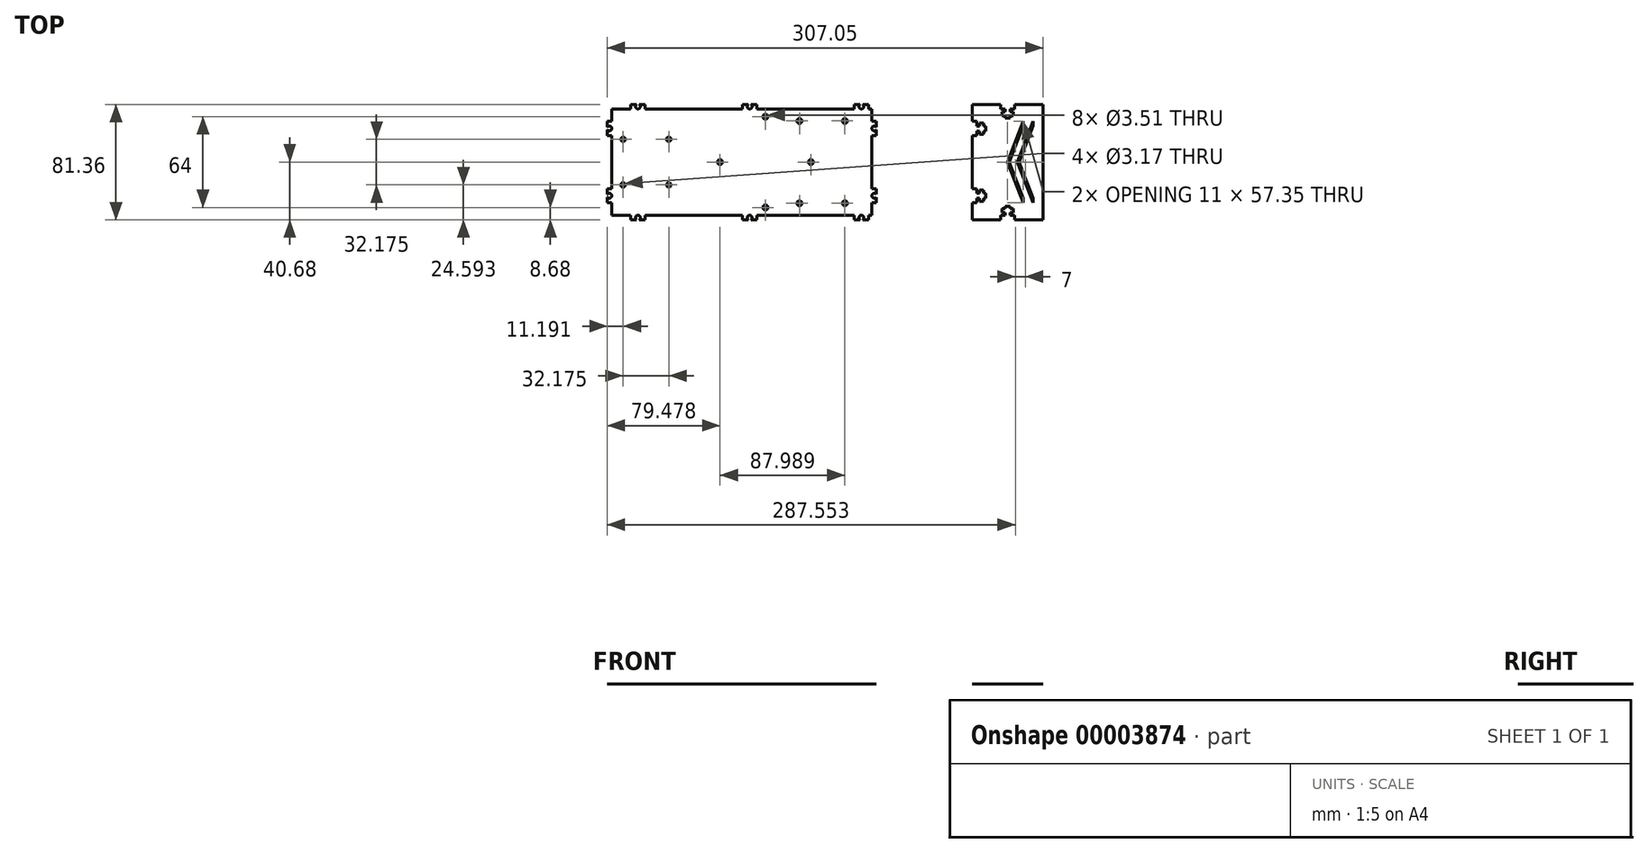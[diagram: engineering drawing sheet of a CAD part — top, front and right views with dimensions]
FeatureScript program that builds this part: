
annotation { "Feature Type Name" : "Feature", "Feature Type Description" : "" }
export const myFeature = defineFeature(function(context is Context, id is Id, definition is map)
    precondition{}
    {
        {
            var Q0;
            Q0=qCreatedBy(makeId("Top.planeOp"),FACE);
            var sketch = newSketch(context, id + "F0", { "sketchPlane" : qUnion([Q0])});
            skLineSegment(sketch, "E0", {"start": v(-129.35, 56.25) * mm, "end": v(-115.88, 56.25) * mm});
            skLineSegment(sketch, "E1", {"start": v(53.99, 56.25) * mm, "end": v(53.99, 47.48) * mm});
            skLineSegment(sketch, "E2", {"start": v(-129.35, 56.25) * mm, "end": v(-129.35, 47.48) * mm});
            skLineSegment(sketch, "E3", {"start": v(-129.35, -18.75) * mm, "end": v(-115.88, -18.75) * mm});
            skPoint(sketch, "E4", {"position": v(-129.35, 18.75) * mm});
            skLineSegment(sketch, "E5", {"start": v(-129.35, 18.75) * mm, "end": v(53.99, 18.75) * mm, "construction": true});
            skPoint(sketch, "E6", {"position": v(-129.35, 37.5) * mm});
            skPoint(sketch, "E7", {"position": v(-129.35, 0) * mm});
            skPoint(sketch, "E8", {"position": v(-129.35, 33.46) * mm});
            skPoint(sketch, "E9", {"position": v(-129.35, 1.3) * mm});
            skPoint(sketch, "E10", {"position": v(-129.35, 56.25) * mm});
            skPoint(sketch, "E11", {"position": v(-129.35, 59.42) * mm});
            skPoint(sketch, "E12", {"position": v(-129.35, -18.75) * mm});
            skPoint(sketch, "E13", {"position": v(-129.35, -21.93) * mm});
            skLineSegment(sketch, "E14", {"start": v(-129.35, 59.42) * mm, "end": v(66.84, 59.42) * mm, "construction": true});
            skPoint(sketch, "E15", {"position": v(-115.88, 56.25) * mm});
            skPoint(sketch, "E16", {"position": v(-105.88, 56.25) * mm});
            skPoint(sketch, "E17", {"position": v(-110.88, 56.25) * mm});
            skArc(sketch, "E18", {"start": v(-111.9, 59.42) * mm, "mid": v(-110.88, 56.25) * mm, "end": v(-109.85, 59.42) * mm});
            skLineSegment(sketch, "E19", {"start": v(-110.88, 58) * mm, "end": v(-110.88, 56.25) * mm});
            skLineSegment(sketch, "E20", {"start": v(-115.88, 56.25) * mm, "end": v(-115.88, 59.42) * mm});
            skLineSegment(sketch, "E21", {"start": v(-115.88, 59.42) * mm, "end": v(-111.9, 59.42) * mm});
            skLineSegment(sketch, "E22", {"start": v(-105.88, 56.25) * mm, "end": v(-105.88, 59.42) * mm});
            skLineSegment(sketch, "E23.trimOffspring", {"start": v(-109.85, 59.42) * mm, "end": v(-105.88, 59.42) * mm});
            skLineSegment(sketch, "E24.0.MirrorCS", {"start": v(-115.88, -18.75) * mm, "end": v(-115.88, -21.93) * mm});
            skLineSegment(sketch, "E25.0.MirrorCS", {"start": v(-115.88, -21.92) * mm, "end": v(-111.9, -21.92) * mm});
            skArc(sketch, "E26.0.MirrorCS", {"start": v(-111.9, -21.93) * mm, "mid": v(-110.88, -18.75) * mm, "end": v(-109.85, -21.93) * mm});
            skLineSegment(sketch, "E27.0.MirrorCS", {"start": v(-109.85, -21.92) * mm, "end": v(-105.88, -21.92) * mm});
            skLineSegment(sketch, "E28.0.MirrorCS", {"start": v(-105.88, -18.75) * mm, "end": v(-105.88, -21.93) * mm});
            skLineSegment(sketch, "E29.trimOffspring", {"start": v(-105.88, 56.25) * mm, "end": v(-37.16, 56.25) * mm});
            skLineSegment(sketch, "E30.trimOffspring", {"start": v(-105.88, -18.75) * mm, "end": v(-37.16, -18.75) * mm});
            skLineSegment(sketch, "E31.1.0.0", {"start": v(-37.16, 56.25) * mm, "end": v(-37.16, 59.42) * mm});
            skLineSegment(sketch, "E31.1.0.1", {"start": v(-37.16, 59.42) * mm, "end": v(-33.18, 59.42) * mm});
            skArc(sketch, "E31.1.0.2", {"start": v(-33.18, 59.42) * mm, "mid": v(-32.16, 56.25) * mm, "end": v(-31.14, 59.42) * mm});
            skLineSegment(sketch, "E31.1.0.3", {"start": v(-31.14, 59.42) * mm, "end": v(-27.16, 59.42) * mm});
            skLineSegment(sketch, "E31.1.0.4", {"start": v(-27.16, 56.25) * mm, "end": v(-27.16, 59.42) * mm});
            skLineSegment(sketch, "E31.2.0.0", {"start": v(41.56, 56.25) * mm, "end": v(41.56, 59.42) * mm});
            skLineSegment(sketch, "E31.2.0.1", {"start": v(41.56, 59.42) * mm, "end": v(45.53, 59.42) * mm});
            skArc(sketch, "E31.2.0.2", {"start": v(45.53, 59.42) * mm, "mid": v(46.56, 56.25) * mm, "end": v(47.58, 59.42) * mm});
            skLineSegment(sketch, "E31.2.0.3", {"start": v(47.58, 59.42) * mm, "end": v(51.56, 59.42) * mm});
            skLineSegment(sketch, "E31.2.0.4", {"start": v(51.56, 56.25) * mm, "end": v(51.56, 59.42) * mm});
            skLineSegment(sketch, "E31.direction1", {"start": v(-115.88, 56.25) * mm, "end": v(-37.16, 56.25) * mm, "construction": true});
            skLineSegment(sketch, "E32.trimOffspring", {"start": v(-27.16, 56.25) * mm, "end": v(41.56, 56.25) * mm});
            skLineSegment(sketch, "E33.trimOffspring", {"start": v(51.56, 56.25) * mm, "end": v(53.99, 56.25) * mm});
            skLineSegment(sketch, "E34.0.MirrorCS", {"start": v(-37.16, -18.75) * mm, "end": v(-37.16, -21.93) * mm});
            skLineSegment(sketch, "E35.0.MirrorCS", {"start": v(-37.16, -21.92) * mm, "end": v(-33.18, -21.92) * mm});
            skArc(sketch, "E36.0.MirrorCS", {"start": v(-33.18, -21.93) * mm, "mid": v(-32.16, -18.75) * mm, "end": v(-31.14, -21.93) * mm});
            skLineSegment(sketch, "E37.0.MirrorCS", {"start": v(-31.14, -21.92) * mm, "end": v(-27.16, -21.92) * mm});
            skLineSegment(sketch, "E38.0.MirrorCS", {"start": v(-27.16, -18.75) * mm, "end": v(-27.16, -21.93) * mm});
            skLineSegment(sketch, "E39.0.MirrorCS", {"start": v(41.56, -18.75) * mm, "end": v(41.56, -21.93) * mm});
            skLineSegment(sketch, "E40.0.MirrorCS", {"start": v(41.56, -21.92) * mm, "end": v(45.53, -21.92) * mm});
            skArc(sketch, "E41.0.MirrorCS", {"start": v(45.53, -21.93) * mm, "mid": v(46.56, -18.75) * mm, "end": v(47.58, -21.93) * mm});
            skLineSegment(sketch, "E42.0.MirrorCS", {"start": v(47.58, -21.92) * mm, "end": v(51.56, -21.92) * mm});
            skLineSegment(sketch, "E43.0.MirrorCS", {"start": v(51.56, -18.75) * mm, "end": v(51.56, -21.93) * mm});
            skLineSegment(sketch, "E44.trimOffspring", {"start": v(51.56, -18.75) * mm, "end": v(53.99, -18.75) * mm});
            skLineSegment(sketch, "E45.trimOffspring", {"start": v(-27.16, -18.75) * mm, "end": v(41.56, -18.75) * mm});
            skPoint(sketch, "E46", {"position": v(57.16, 52.54) * mm});
            skLineSegment(sketch, "E47", {"start": v(57.16, 65.35) * mm, "end": v(57.16, -30) * mm, "construction": true});
            skPoint(sketch, "E48", {"position": v(53.99, 47.48) * mm});
            skPoint(sketch, "E49", {"position": v(53.99, 37.48) * mm});
            skPoint(sketch, "E50", {"position": v(53.99, 42.48) * mm});
            skArc(sketch, "E51", {"start": v(57.16, 43.5) * mm, "mid": v(53.99, 42.48) * mm, "end": v(57.16, 41.46) * mm});
            skLineSegment(sketch, "E52", {"start": v(55.74, 42.48) * mm, "end": v(53.99, 42.48) * mm});
            skLineSegment(sketch, "E53", {"start": v(53.99, 37.48) * mm, "end": v(57.16, 37.48) * mm});
            skLineSegment(sketch, "E54", {"start": v(57.16, 37.48) * mm, "end": v(57.16, 41.46) * mm});
            skLineSegment(sketch, "E55", {"start": v(57.16, 47.48) * mm, "end": v(53.99, 47.48) * mm});
            skLineSegment(sketch, "E56.trimOffspring", {"start": v(53.99, 37.48) * mm, "end": v(53.99, 0.02) * mm});
            skLineSegment(sketch, "E57.trimOffspring", {"start": v(57.16, 43.5) * mm, "end": v(57.16, 47.48) * mm});
            skLineSegment(sketch, "E58.0.MirrorCS", {"start": v(53.99, 0.02) * mm, "end": v(57.16, 0.02) * mm});
            skLineSegment(sketch, "E59.0.MirrorCS", {"start": v(57.16, 0.02) * mm, "end": v(57.16, -3.96) * mm});
            skArc(sketch, "E60.0.MirrorCS", {"start": v(57.16, -6) * mm, "mid": v(53.99, -4.98) * mm, "end": v(57.16, -3.96) * mm});
            skLineSegment(sketch, "E61.0.MirrorCS", {"start": v(57.16, -6) * mm, "end": v(57.16, -9.98) * mm});
            skLineSegment(sketch, "E62.0.MirrorCS", {"start": v(57.16, -9.98) * mm, "end": v(53.99, -9.98) * mm});
            skLineSegment(sketch, "E63.trimOffspring", {"start": v(53.99, -9.98) * mm, "end": v(53.99, -18.75) * mm});
            skLineSegment(sketch, "E64", {"start": v(124.52, -18.75) * mm, "end": v(174.52, -18.75) * mm, "construction": true});
            skLineSegment(sketch, "E65", {"start": v(174.52, -18.75) * mm, "end": v(174.52, 56.25) * mm, "construction": true});
            skLineSegment(sketch, "E66", {"start": v(174.52, 56.25) * mm, "end": v(147.77, 56.25) * mm, "construction": true});
            skLineSegment(sketch, "E67", {"start": v(124.52, 56.25) * mm, "end": v(124.52, -18.75) * mm, "construction": true});
            skLineSegment(sketch, "E68", {"start": v(124.52, 56.25) * mm, "end": v(124.52, 47.48) * mm});
            skLineSegment(sketch, "E69", {"start": v(174.52, -18.75) * mm, "end": v(174.52, 56.25) * mm});
            skLineSegment(sketch, "E70", {"start": v(57.16, 42.48) * mm, "end": v(53.99, 42.48) * mm, "construction": true});
            skPoint(sketch, "E71", {"position": v(127.7, 56.25) * mm});
            skLineSegment(sketch, "E72", {"start": v(127.7, 56.25) * mm, "end": v(127.7, 44.24) * mm, "construction": true});
            skPoint(sketch, "E73", {"position": v(129.68, 56.25) * mm});
            skPoint(sketch, "E74", {"position": v(132.46, 56.25) * mm});
            skPoint(sketch, "E75", {"position": v(134.05, 56.25) * mm});
            skPoint(sketch, "E76", {"position": v(149.52, -18.75) * mm});
            skLineSegment(sketch, "E77", {"start": v(149.52, -18.75) * mm, "end": v(149.52, 56.25) * mm, "construction": true});
            skLineSegment(sketch, "E78", {"start": v(129.68, 56.25) * mm, "end": v(129.68, 44.24) * mm, "construction": true});
            skLineSegment(sketch, "E79", {"start": v(132.46, 56.25) * mm, "end": v(132.46, 44.24) * mm, "construction": true});
            skLineSegment(sketch, "E80", {"start": v(134.05, 56.25) * mm, "end": v(134.05, -18.75) * mm, "construction": true});
            skPoint(sketch, "E81", {"position": v(124.52, 44.24) * mm});
            skPoint(sketch, "E82.0.MirrorP", {"position": v(124.52, 40.73) * mm});
            skLineSegment(sketch, "E83", {"start": v(127.7, 44.24) * mm, "end": v(129.68, 44.24) * mm, "construction": true});
            skLineSegment(sketch, "E84", {"start": v(127.7, 40.73) * mm, "end": v(129.68, 40.73) * mm, "construction": true});
            skLineSegment(sketch, "E85", {"start": v(124.52, 47.48) * mm, "end": v(127.7, 47.48) * mm});
            skLineSegment(sketch, "E86", {"start": v(124.52, 37.48) * mm, "end": v(127.7, 37.48) * mm});
            skLineSegment(sketch, "E87", {"start": v(127.7, 37.48) * mm, "end": v(127.7, 40.73) * mm});
            skLineSegment(sketch, "E88", {"start": v(127.7, 44.24) * mm, "end": v(129.68, 44.24) * mm});
            skPoint(sketch, "E89", {"position": v(129.68, 46.45) * mm});
            skPoint(sketch, "E90.0.MirrorP", {"position": v(129.68, 38.51) * mm});
            skLineSegment(sketch, "E91", {"start": v(129.68, 46.45) * mm, "end": v(132.46, 46.45) * mm});
            skLineSegment(sketch, "E92", {"start": v(129.68, 38.51) * mm, "end": v(132.46, 38.51) * mm});
            skLineSegment(sketch, "E93", {"start": v(129.68, 38.51) * mm, "end": v(129.68, 40.73) * mm});
            skLineSegment(sketch, "E94", {"start": v(129.68, 46.45) * mm, "end": v(129.68, 44.24) * mm});
            skLineSegment(sketch, "E95", {"start": v(127.7, 40.73) * mm, "end": v(129.68, 40.73) * mm});
            skLineSegment(sketch, "E96.trimOffspring", {"start": v(127.7, 44.24) * mm, "end": v(127.7, 47.48) * mm});
            skLineSegment(sketch, "E97", {"start": v(132.46, 46.45) * mm, "end": v(132.46, 44.24) * mm});
            skLineSegment(sketch, "E98", {"start": v(132.46, 44.24) * mm, "end": v(134.05, 44.24) * mm});
            skLineSegment(sketch, "E99", {"start": v(134.05, 44.24) * mm, "end": v(134.05, 40.73) * mm});
            skLineSegment(sketch, "E100", {"start": v(134.05, 40.73) * mm, "end": v(132.46, 40.73) * mm});
            skLineSegment(sketch, "E101", {"start": v(132.46, 40.73) * mm, "end": v(132.46, 38.51) * mm});
            skLineSegment(sketch, "E102.trimOffspring", {"start": v(127.7, 40.73) * mm, "end": v(127.7, -18.75) * mm, "construction": true});
            skLineSegment(sketch, "E103.trimOffspring", {"start": v(129.68, 40.73) * mm, "end": v(129.68, -18.75) * mm, "construction": true});
            skLineSegment(sketch, "E104.trimOffspring", {"start": v(124.52, 37.48) * mm, "end": v(124.52, 0.02) * mm});
            skLineSegment(sketch, "E105.trimOffspring", {"start": v(132.46, 44.24) * mm, "end": v(134.05, 44.24) * mm, "construction": true});
            skLineSegment(sketch, "E106.trimOffspring", {"start": v(132.46, 40.73) * mm, "end": v(132.46, -18.75) * mm, "construction": true});
            skLineSegment(sketch, "E107.trimOffspring", {"start": v(132.46, 40.73) * mm, "end": v(134.05, 40.73) * mm, "construction": true});
            skLineSegment(sketch, "E108", {"start": v(124.52, 18.75) * mm, "end": v(174.52, 18.75) * mm, "construction": true});
            skLineSegment(sketch, "E109.0.MirrorCS", {"start": v(124.52, 0.02) * mm, "end": v(127.7, 0.02) * mm});
            skLineSegment(sketch, "E110.0.MirrorCS", {"start": v(127.7, 0.02) * mm, "end": v(127.7, -3.23) * mm});
            skLineSegment(sketch, "E111.0.MirrorCS", {"start": v(127.7, -3.23) * mm, "end": v(129.68, -3.23) * mm});
            skLineSegment(sketch, "E112.0.MirrorCS", {"start": v(129.68, -1.01) * mm, "end": v(129.68, -3.23) * mm});
            skLineSegment(sketch, "E113.0.MirrorCS", {"start": v(129.68, -1.01) * mm, "end": v(132.46, -1.01) * mm});
            skLineSegment(sketch, "E114.0.MirrorCS", {"start": v(132.46, -3.23) * mm, "end": v(132.46, -1.01) * mm});
            skLineSegment(sketch, "E115.0.MirrorCS", {"start": v(134.05, -3.23) * mm, "end": v(132.46, -3.23) * mm});
            skLineSegment(sketch, "E116.0.MirrorCS", {"start": v(134.05, -6.74) * mm, "end": v(134.05, -3.23) * mm});
            skLineSegment(sketch, "E117.0.MirrorCS", {"start": v(132.46, -6.74) * mm, "end": v(134.05, -6.74) * mm});
            skLineSegment(sketch, "E118.0.MirrorCS", {"start": v(132.46, -8.95) * mm, "end": v(132.46, -6.74) * mm});
            skLineSegment(sketch, "E119.0.MirrorCS", {"start": v(129.68, -8.95) * mm, "end": v(132.46, -8.95) * mm});
            skLineSegment(sketch, "E120.0.MirrorCS", {"start": v(129.68, -8.95) * mm, "end": v(129.68, -6.74) * mm});
            skLineSegment(sketch, "E121.0.MirrorCS", {"start": v(127.7, -6.74) * mm, "end": v(127.7, -9.98) * mm});
            skLineSegment(sketch, "E122.0.MirrorCS", {"start": v(124.52, -9.98) * mm, "end": v(127.7, -9.98) * mm});
            skLineSegment(sketch, "E123.0.MirrorCS", {"start": v(127.7, -6.74) * mm, "end": v(129.68, -6.74) * mm});
            skLineSegment(sketch, "E124.trimOffspring", {"start": v(124.52, -9.98) * mm, "end": v(124.52, -18.75) * mm});
            skPoint(sketch, "E125", {"position": v(34.94, 56.25) * mm});
            skPoint(sketch, "E126", {"position": v(24.94, 56.25) * mm});
            skPoint(sketch, "E127", {"position": v(18.94, 56.25) * mm});
            skPoint(sketch, "E128", {"position": v(12.94, 56.25) * mm});
            skPoint(sketch, "E129", {"position": v(2.94, 56.25) * mm});
            skPoint(sketch, "E130", {"position": v(2.94, 47.75) * mm});
            skPoint(sketch, "E131", {"position": v(34.94, 47.75) * mm});
            skCircle(sketch, "E132", {"center": v(2.94, 47.75) * mm, "radius": 1.75 * mm});
            skCircle(sketch, "E133", {"center": v(34.94, 47.75) * mm, "radius": 1.75 * mm});
            skCircle(sketch, "E134.0.MirrorC", {"center": v(2.94, -10.25) * mm, "radius": 1.75 * mm});
            skCircle(sketch, "E135.0.MirrorC", {"center": v(34.94, -10.25) * mm, "radius": 1.75 * mm});
            skPoint(sketch, "E136.0.MirrorP", {"position": v(12.94, -18.75) * mm});
            skPoint(sketch, "E137.0.MirrorP", {"position": v(18.94, -18.75) * mm});
            skPoint(sketch, "E138.0.MirrorP", {"position": v(24.94, -18.75) * mm});
            skPoint(sketch, "E139", {"position": v(153.5, 56.25) * mm});
            skPoint(sketch, "E140", {"position": v(154.52, 56.25) * mm});
            skPoint(sketch, "E141", {"position": v(149.52, 53.08) * mm});
            skPoint(sketch, "E142", {"position": v(149.52, 51.1) * mm});
            skPoint(sketch, "E143", {"position": v(149.52, 48.31) * mm});
            skPoint(sketch, "E144", {"position": v(149.52, 46.73) * mm});
            skPoint(sketch, "E145.0.MirrorP", {"position": v(145.55, 56.25) * mm});
            skPoint(sketch, "E146.0.MirrorP", {"position": v(144.52, 56.25) * mm});
            skPoint(sketch, "E147", {"position": v(151.28, 56.25) * mm});
            skPoint(sketch, "E148.0.MirrorP", {"position": v(147.77, 56.25) * mm});
            skLineSegment(sketch, "E149", {"start": v(151.28, 51.49) * mm, "end": v(151.28, 51.1) * mm});
            skLineSegment(sketch, "E150.0.MirrorCS", {"start": v(144.52, 53.08) * mm, "end": v(147.77, 53.08) * mm});
            skLineSegment(sketch, "E151.0.MirrorCS", {"start": v(147.77, 51.49) * mm, "end": v(147.77, 51.1) * mm});
            skLineSegment(sketch, "E152.trimOffspring", {"start": v(151.28, 56.25) * mm, "end": v(153.5, 56.25) * mm});
            skLineSegment(sketch, "E153.trimOffspring", {"start": v(144.52, 56.25) * mm, "end": v(124.52, 56.25) * mm, "construction": true});
            skLineSegment(sketch, "E154.0.MirrorCS", {"start": v(151.28, -15.57) * mm, "end": v(151.28, -13.6) * mm});
            skLineSegment(sketch, "E155.0.MirrorCS", {"start": v(147.77, -13.99) * mm, "end": v(147.77, -13.6) * mm});
            skPoint(sketch, "E156", {"position": v(-129.3, -90.32) * mm});
            skPoint(sketch, "E157", {"position": v(174.52, 44.25) * mm});
            skPoint(sketch, "E158", {"position": v(174.52, -6.75) * mm});
            skPoint(sketch, "E159", {"position": v(160.52, 56.25) * mm});
            skPoint(sketch, "E160", {"position": v(167.52, 56.25) * mm});
            skPoint(sketch, "E161", {"position": v(174.52, 47.43) * mm});
            skLineSegment(sketch, "E162", {"start": v(160.52, 47.43) * mm, "end": v(167.52, 47.43) * mm, "construction": true});
            skLineSegment(sketch, "E163", {"start": v(167.52, 47.43) * mm, "end": v(167.52, 44.25) * mm, "construction": true});
            skLineSegment(sketch, "E164", {"start": v(53.99, 42.48) * mm, "end": v(57.16, 42.48) * mm, "construction": true});
            skLineSegment(sketch, "E165", {"start": v(55.74, -4.98) * mm, "end": v(-129.35, -4.98) * mm, "construction": true});
            skPoint(sketch, "E166", {"position": v(-129.35, 0.02) * mm});
            skPoint(sketch, "E167", {"position": v(-129.35, -9.98) * mm});
            skPoint(sketch, "E168", {"position": v(-132.53, -9.98) * mm});
            skLineSegment(sketch, "E169", {"start": v(-129.35, -9.98) * mm, "end": v(-132.53, -9.98) * mm});
            skLineSegment(sketch, "E170", {"start": v(-132.53, -9.98) * mm, "end": v(-132.53, -6) * mm});
            skLineSegment(sketch, "E171", {"start": v(-132.53, 0) * mm, "end": v(-129.35, 0) * mm});
            skArc(sketch, "E172", {"start": v(-132.53, -6) * mm, "mid": v(-129.35, -4.98) * mm, "end": v(-132.53, -3.96) * mm});
            skLineSegment(sketch, "E173.trimOffspring", {"start": v(-129.35, -9.98) * mm, "end": v(-129.35, -18.75) * mm});
            skLineSegment(sketch, "E174.trimOffspring", {"start": v(-132.53, -3.96) * mm, "end": v(-132.53, 0) * mm});
            skLineSegment(sketch, "E175", {"start": v(53.99, 42.48) * mm, "end": v(-129.35, 42.48) * mm, "construction": true});
            skPoint(sketch, "E176", {"position": v(-129.35, 47.48) * mm});
            skPoint(sketch, "E177", {"position": v(-129.35, 37.48) * mm});
            skPoint(sketch, "E178", {"position": v(-132.53, 37.5) * mm});
            skLineSegment(sketch, "E179", {"start": v(-129.35, 37.5) * mm, "end": v(-132.53, 37.5) * mm});
            skLineSegment(sketch, "E180", {"start": v(-132.53, 37.5) * mm, "end": v(-132.53, 41.46) * mm});
            skLineSegment(sketch, "E181", {"start": v(-132.53, 47.48) * mm, "end": v(-129.35, 47.48) * mm});
            skArc(sketch, "E182", {"start": v(-132.53, 41.46) * mm, "mid": v(-129.35, 42.48) * mm, "end": v(-132.53, 43.5) * mm});
            skLineSegment(sketch, "E183", {"start": v(-131.1, 42.48) * mm, "end": v(-129.35, 42.48) * mm});
            skLineSegment(sketch, "E184.trimOffspring", {"start": v(-129.35, 37.5) * mm, "end": v(-129.35, 0) * mm});
            skLineSegment(sketch, "E185", {"start": v(-129.35, 56.25) * mm, "end": v(-129.35, 42.48) * mm});
            skLineSegment(sketch, "E186.trimOffspring", {"start": v(-132.53, 43.5) * mm, "end": v(-132.53, 47.48) * mm});
            skPoint(sketch, "E187", {"position": v(10.95, 18.75) * mm});
            skPoint(sketch, "E188", {"position": v(-53.05, 18.75) * mm});
            skPoint(sketch, "E189", {"position": v(-21.05, 18.75) * mm});
            skPoint(sketch, "E190", {"position": v(4.45, 18.75) * mm});
            skPoint(sketch, "E191", {"position": v(-46.55, 18.75) * mm});
            skCircle(sketch, "E192", {"center": v(-53.05, 18.75) * mm, "radius": 1.75 * mm});
            skCircle(sketch, "E193", {"center": v(10.95, 18.75) * mm, "radius": 1.75 * mm});
            skPoint(sketch, "E194", {"position": v(-21.05, 50.75) * mm});
            skPoint(sketch, "E195", {"position": v(-21.05, -13.25) * mm});
            skCircle(sketch, "E196", {"center": v(-21.05, 50.75) * mm, "radius": 1.75 * mm});
            skCircle(sketch, "E197", {"center": v(-21.05, -13.25) * mm, "radius": 1.75 * mm});
            skPoint(sketch, "E198.0.MirrorCS.start.orphan", {"position": v(160.52, -9.92) * mm});
            skPoint(sketch, "E199.0.MirrorCS.start.orphan", {"position": v(160.52, -6.75) * mm});
            skPoint(sketch, "E200.0.MirrorCS.end.orphan", {"position": v(167.52, -6.75) * mm});
            skPoint(sketch, "E200.0.MirrorCS.start.orphan", {"position": v(167.52, -9.92) * mm});
            skPoint(sketch, "E201.start.orphan", {"position": v(160.52, 44.25) * mm});
            skPoint(sketch, "E202", {"position": v(149.52, 18.75) * mm});
            skLineSegment(sketch, "E203", {"start": v(160.52, -9.92) * mm, "end": v(149.52, 18.75) * mm});
            skLineSegment(sketch, "E204", {"start": v(149.52, 18.75) * mm, "end": v(160.52, 47.42) * mm});
            skLineSegment(sketch, "E205", {"start": v(160.52, 44.25) * mm, "end": v(150.74, 18.75) * mm});
            skLineSegment(sketch, "E206", {"start": v(150.74, 18.75) * mm, "end": v(160.52, -6.75) * mm});
            skPoint(sketch, "E207", {"position": v(156.52, 18.75) * mm});
            skLineSegment(sketch, "E208", {"start": v(167.52, 47.43) * mm, "end": v(156.52, 18.75) * mm});
            skLineSegment(sketch, "E209", {"start": v(156.52, 18.75) * mm, "end": v(167.52, -9.92) * mm});
            skLineSegment(sketch, "E210", {"start": v(167.52, 44.25) * mm, "end": v(157.74, 18.75) * mm});
            skLineSegment(sketch, "E211", {"start": v(157.74, 18.75) * mm, "end": v(167.52, -6.75) * mm});
            skLineSegment(sketch, "E212", {"start": v(167.52, -6.75) * mm, "end": v(167.52, -9.92) * mm});
            skLineSegment(sketch, "E213", {"start": v(160.52, -9.92) * mm, "end": v(160.52, -6.75) * mm});
            skLineSegment(sketch, "E214", {"start": v(160.52, 44.25) * mm, "end": v(160.52, 47.43) * mm});
            skLineSegment(sketch, "E215", {"start": v(167.52, 44.25) * mm, "end": v(167.52, 47.43) * mm});
            skPoint(sketch, "E216.orphan", {"position": v(124.52, 42.48) * mm});
            skLineSegment(sketch, "E217.trimOffspring", {"start": v(124.52, 42.48) * mm, "end": v(174.52, 42.48) * mm, "construction": true});
            skLineSegment(sketch, "E218.0.1.0", {"start": v(154.52, -21.92) * mm, "end": v(154.52, -18.75) * mm});
            skLineSegment(sketch, "E218.0.1.1", {"start": v(154.52, -18.75) * mm, "end": v(151.28, -18.75) * mm});
            skLineSegment(sketch, "E218.0.1.2", {"start": v(151.28, -18.75) * mm, "end": v(151.28, -16.77) * mm});
            skLineSegment(sketch, "E218.0.1.3", {"start": v(151.28, -16.77) * mm, "end": v(153.5, -16.77) * mm});
            skLineSegment(sketch, "E218.0.1.4", {"start": v(153.5, -16.77) * mm, "end": v(153.5, -13.99) * mm});
            skLineSegment(sketch, "E218.0.1.5", {"start": v(153.5, -13.99) * mm, "end": v(151.28, -13.99) * mm});
            skLineSegment(sketch, "E218.0.1.6", {"start": v(151.28, -13.99) * mm, "end": v(151.28, -12.4) * mm});
            skLineSegment(sketch, "E218.0.1.7", {"start": v(151.28, -12.4) * mm, "end": v(149.52, -12.4) * mm});
            skLineSegment(sketch, "E218.0.1.8", {"start": v(147.77, -12.4) * mm, "end": v(149.52, -12.4) * mm});
            skLineSegment(sketch, "E218.0.1.9", {"start": v(147.77, -13.99) * mm, "end": v(147.77, -12.4) * mm});
            skLineSegment(sketch, "E218.0.1.10", {"start": v(145.55, -13.99) * mm, "end": v(147.77, -13.99) * mm});
            skLineSegment(sketch, "E218.0.1.11", {"start": v(145.55, -16.77) * mm, "end": v(145.55, -13.99) * mm});
            skLineSegment(sketch, "E218.0.1.12", {"start": v(147.77, -16.77) * mm, "end": v(145.55, -16.77) * mm});
            skLineSegment(sketch, "E218.0.1.13", {"start": v(147.77, -18.75) * mm, "end": v(147.77, -16.77) * mm});
            skLineSegment(sketch, "E218.0.1.14", {"start": v(144.52, -18.75) * mm, "end": v(147.77, -18.75) * mm});
            skLineSegment(sketch, "E218.0.1.15", {"start": v(144.52, -21.92) * mm, "end": v(144.52, -18.75) * mm});
            skLineSegment(sketch, "E218.direction2", {"start": v(154.52, -18.75) * mm, "end": v(154.52, -21.92) * mm, "construction": true});
            skLineSegment(sketch, "E219", {"start": v(144.52, -21.92) * mm, "end": v(124.52, -21.92) * mm});
            skLineSegment(sketch, "E220", {"start": v(124.52, -21.92) * mm, "end": v(124.52, -18.75) * mm});
            skPoint(sketch, "E221.orphan", {"position": v(144.52, -18.75) * mm});
            skLineSegment(sketch, "E222", {"start": v(154.52, -21.93) * mm, "end": v(174.52, -21.93) * mm});
            skLineSegment(sketch, "E223", {"start": v(174.52, -21.93) * mm, "end": v(174.52, -18.75) * mm});
            skLineSegment(sketch, "E224.0.1.0", {"start": v(144.52, 59.42) * mm, "end": v(144.52, 56.25) * mm});
            skLineSegment(sketch, "E224.0.1.1", {"start": v(144.52, 56.25) * mm, "end": v(147.77, 56.25) * mm});
            skLineSegment(sketch, "E224.0.1.2", {"start": v(147.77, 56.25) * mm, "end": v(147.77, 54.27) * mm});
            skLineSegment(sketch, "E224.0.1.3", {"start": v(147.77, 54.27) * mm, "end": v(145.55, 54.27) * mm});
            skLineSegment(sketch, "E224.0.1.4", {"start": v(145.55, 54.27) * mm, "end": v(145.55, 51.49) * mm});
            skLineSegment(sketch, "E224.0.1.5", {"start": v(145.55, 51.49) * mm, "end": v(147.77, 51.49) * mm});
            skLineSegment(sketch, "E224.0.1.6", {"start": v(147.77, 51.49) * mm, "end": v(147.77, 49.9) * mm});
            skLineSegment(sketch, "E224.0.1.7", {"start": v(147.77, 49.9) * mm, "end": v(149.52, 49.9) * mm});
            skLineSegment(sketch, "E224.0.1.8", {"start": v(151.28, 49.9) * mm, "end": v(149.52, 49.9) * mm});
            skLineSegment(sketch, "E224.0.1.9", {"start": v(151.28, 51.49) * mm, "end": v(151.28, 49.9) * mm});
            skLineSegment(sketch, "E224.0.1.10", {"start": v(153.5, 51.49) * mm, "end": v(151.28, 51.49) * mm});
            skLineSegment(sketch, "E224.0.1.11", {"start": v(153.5, 54.27) * mm, "end": v(153.5, 51.49) * mm});
            skLineSegment(sketch, "E224.0.1.12", {"start": v(151.28, 54.27) * mm, "end": v(153.5, 54.27) * mm});
            skLineSegment(sketch, "E224.0.1.13", {"start": v(151.28, 56.25) * mm, "end": v(151.28, 54.27) * mm});
            skLineSegment(sketch, "E224.0.1.14", {"start": v(154.52, 56.25) * mm, "end": v(151.28, 56.25) * mm});
            skLineSegment(sketch, "E224.0.1.15", {"start": v(154.52, 59.42) * mm, "end": v(154.52, 56.25) * mm});
            skPoint(sketch, "E224.0.1.16", {"position": v(174.52, 50.6) * mm});
            skLineSegment(sketch, "E224.direction1", {"start": v(144.52, 53.08) * mm, "end": v(169.52, 53.08) * mm, "construction": true});
            skLineSegment(sketch, "E224.direction2", {"start": v(144.52, 53.08) * mm, "end": v(144.52, 56.25) * mm, "construction": true});
            skPoint(sketch, "E225.0.MirrorCS.end.orphan", {"position": v(147.77, 46.73) * mm});
            skPoint(sketch, "E226.0.MirrorCS.end.orphan", {"position": v(147.77, 48.31) * mm});
            skPoint(sketch, "E227.0.MirrorCS.end.orphan", {"position": v(145.55, 48.31) * mm});
            skPoint(sketch, "E227.0.MirrorCS.start.orphan", {"position": v(145.55, 51.1) * mm});
            skPoint(sketch, "E228.end.orphan", {"position": v(151.28, 46.73) * mm});
            skPoint(sketch, "E229.end.orphan", {"position": v(151.28, 48.31) * mm});
            skPoint(sketch, "E230.end.orphan", {"position": v(153.5, 48.31) * mm});
            skPoint(sketch, "E231.end.orphan", {"position": v(153.5, 51.1) * mm});
            skLineSegment(sketch, "E232", {"start": v(144.52, 59.42) * mm, "end": v(124.52, 59.42) * mm});
            skLineSegment(sketch, "E233", {"start": v(124.52, 59.42) * mm, "end": v(124.52, 56.25) * mm});
            skLineSegment(sketch, "E234", {"start": v(154.52, 59.42) * mm, "end": v(174.52, 59.42) * mm});
            skLineSegment(sketch, "E235", {"start": v(174.52, 59.42) * mm, "end": v(174.52, 56.25) * mm});
            skPoint(sketch, "E236.orphan", {"position": v(154.52, 53.08) * mm});
            skPoint(sketch, "E237.end.orphan", {"position": v(151.28, 53.08) * mm});
            skPoint(sketch, "E238", {"position": v(-121.34, 18.75) * mm});
            skCircle(sketch, "E239", {"center": v(-121.34, 2.66) * mm, "radius": 1.59 * mm});
            skPoint(sketch, "E240", {"position": v(-121.34, 4.25) * mm});
            skPoint(sketch, "E241", {"position": v(-119.75, 2.66) * mm});
            skCircle(sketch, "E242", {"center": v(-89.16, 2.66) * mm, "radius": 1.59 * mm});
            skPoint(sketch, "E243", {"position": v(-89.16, 4.25) * mm});
            skPoint(sketch, "E244", {"position": v(-90.75, 2.66) * mm});
            skCircle(sketch, "E245.0.MirrorC", {"center": v(-121.34, 34.84) * mm, "radius": 1.59 * mm});
            skCircle(sketch, "E246.0.MirrorC", {"center": v(-89.16, 34.84) * mm, "radius": 1.59 * mm});
            skSolve(sketch);
        }
        {
            var Q0;
            Q0 = qSketchRegion(id + "F0", true);
            extrude(context, id + "F1", {"entities" : qUnion([Q0]), "depth" : 1 / 203.2 * mm});
        }
    });
